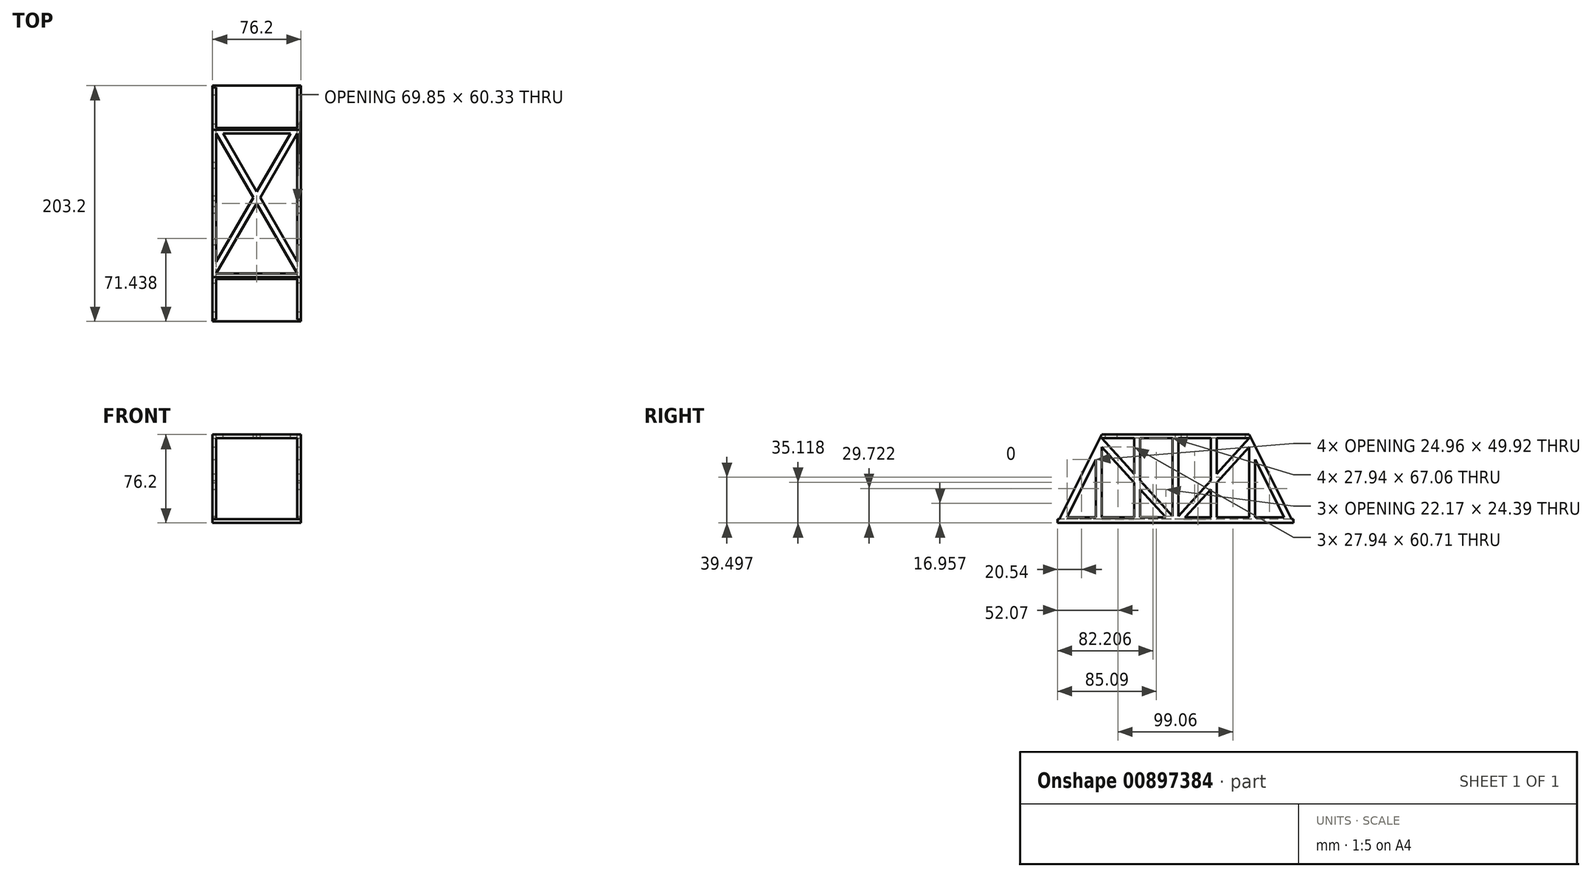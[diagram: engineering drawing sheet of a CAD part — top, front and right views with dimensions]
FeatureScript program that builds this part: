
annotation { "Feature Type Name" : "Feature", "Feature Type Description" : "" }
export const myFeature = defineFeature(function(context is Context, id is Id, definition is map)
    precondition{}
    {
        {
            var Q0;
            Q0=qCreatedBy(makeId("Right.planeOp"),FACE);
            var sketch = newSketch(context, id + "F0", { "sketchPlane" : qUnion([Q0])});
            skLineSegment(sketch, "E0", {"start": v(-101.6, -38.1) * mm, "end": v(101.6, -38.1) * mm});
            skLineSegment(sketch, "E1", {"start": v(-63.5, 38.1) * mm, "end": v(63.5, 38.1) * mm});
            skLineSegment(sketch, "E2", {"start": v(-101.6, -38.1) * mm, "end": v(-63.5, 38.1) * mm});
            skLineSegment(sketch, "E3", {"start": v(63.5, 38.1) * mm, "end": v(101.6, -38.1) * mm});
            skSolve(sketch);
        }
        {
            var Q0;
            Q0 = qSketchRegion(id + "F0", true);
            extrude(context, id + "F1", {"entities" : qUnion([Q0]), "endBound" : BoundingType.SYMMETRIC, "depth" : 76.2 * mm, "offsetDistance" : 25.4 * mm});
        }
        {
            var Q0;
            Q0=makeQuery(id+"F1.opExtrude","CAP_FACE",FACE,{"disambiguationData":[OSD([sQuery(id+"F0.wireOp",EDGE,"E0"),sQuery(id+"F0.wireOp",EDGE,"E1"),sQuery(id+"F0.wireOp",EDGE,"E2"),sQuery(id+"F0.wireOp",EDGE,"E3")])],"isStart":false});
            var sketch = newSketch(context, id + "F2", { "sketchPlane" : qUnion([Q0])});
            skLineSegment(sketch, "E4", {"start": v(-63.5, 34.92) * mm, "end": v(-63.5, -34.93) * mm});
            skLineSegment(sketch, "E5", {"start": v(-63.5, -34.93) * mm, "end": v(63.5, -34.93) * mm});
            skLineSegment(sketch, "E6", {"start": v(63.5, -34.93) * mm, "end": v(63.5, 34.93) * mm});
            skLineSegment(sketch, "E7", {"start": v(63.5, 34.93) * mm, "end": v(-63.5, 34.92) * mm});
            skLineSegment(sketch, "E8", {"start": v(-63.5, 34.93) * mm, "end": v(0, -34.93) * mm});
            skLineSegment(sketch, "E9", {"start": v(0, -34.92) * mm, "end": v(63.5, 34.93) * mm});
            skLineSegment(sketch, "E10", {"start": v(-63.5, 27.37) * mm, "end": v(-6.87, -34.93) * mm});
            skLineSegment(sketch, "E11", {"start": v(63.5, 27.37) * mm, "end": v(6.87, -34.93) * mm});
            skLineSegment(sketch, "E12", {"start": v(-68.58, 16.58) * mm, "end": v(-68.58, -34.93) * mm});
            skLineSegment(sketch, "E13", {"start": v(-68.58, 16.58) * mm, "end": v(-94.33, -34.93) * mm});
            skLineSegment(sketch, "E14", {"start": v(-94.33, -34.93) * mm, "end": v(-68.58, -34.93) * mm});
            skLineSegment(sketch, "E15.MirrorCS", {"start": v(68.58, 16.58) * mm, "end": v(68.58, -34.93) * mm});
            skLineSegment(sketch, "E16.MirrorCS", {"start": v(68.58, 16.58) * mm, "end": v(94.33, -34.93) * mm});
            skLineSegment(sketch, "E17.MirrorCS", {"start": v(94.33, -34.93) * mm, "end": v(68.58, -34.93) * mm});
            skLineSegment(sketch, "E18.bottom", {"start": v(2.54, -34.93) * mm, "end": v(-2.54, -34.93) * mm});
            skLineSegment(sketch, "E18.top", {"start": v(2.54, 34.93) * mm, "end": v(-2.54, 34.93) * mm});
            skLineSegment(sketch, "E18.left", {"start": v(2.54, -34.92) * mm, "end": v(2.54, 34.92) * mm});
            skLineSegment(sketch, "E18.right", {"start": v(-2.54, -34.92) * mm, "end": v(-2.54, 34.92) * mm});
            skPoint(sketch, "E18.middle", {"position": v(0, 0) * mm});
            skLineSegment(sketch, "E19.bottom", {"start": v(-30.48, -34.93) * mm, "end": v(-35.56, -34.93) * mm});
            skLineSegment(sketch, "E19.top", {"start": v(-30.48, 34.93) * mm, "end": v(-35.56, 34.93) * mm});
            skLineSegment(sketch, "E19.left", {"start": v(-30.48, -34.93) * mm, "end": v(-30.48, 34.93) * mm});
            skLineSegment(sketch, "E19.right", {"start": v(-35.56, -34.93) * mm, "end": v(-35.56, 34.93) * mm});
            skPoint(sketch, "E19.middle", {"position": v(-33.02, 0) * mm});
            skLineSegment(sketch, "E20.MirrorCS", {"start": v(35.56, -34.93) * mm, "end": v(35.56, 34.93) * mm});
            skLineSegment(sketch, "E21.MirrorCS", {"start": v(30.48, -34.93) * mm, "end": v(30.48, 34.93) * mm});
            skSolve(sketch);
        }
        {
            var Q0;
            Q0=qCreatedBy(makeId("Front.planeOp"),FACE);
            var sketch = newSketch(context, id + "F3", { "sketchPlane" : qUnion([Q0])});
            skLineSegment(sketch, "E22.bottom", {"start": v(34.93, -34.93) * mm, "end": v(-34.93, -34.93) * mm});
            skLineSegment(sketch, "E22.top", {"start": v(34.93, 34.93) * mm, "end": v(-34.93, 34.93) * mm});
            skLineSegment(sketch, "E22.left", {"start": v(34.93, -34.93) * mm, "end": v(34.93, 34.93) * mm});
            skLineSegment(sketch, "E22.right", {"start": v(-34.93, -34.93) * mm, "end": v(-34.93, 34.93) * mm});
            skPoint(sketch, "E22.middle", {"position": v(0, 0) * mm});
            skSolve(sketch);
        }
        {
            var Q0;
            Q0 = qSketchRegion(id + "F3", true);
            extrude(context, id + "F4", {"entities" : qUnion([Q0]), "operationType" : NewBodyOperationType.REMOVE, "endBound" : BoundingType.SYMMETRIC, "oppositeDirection" : true, "depth" : 254 * mm, "offsetDistance" : 25.4 * mm});
        }
        {
            var Q0;
            Q0=makeQuery(id+"F2.imprint","IMPRINT",FACE,{"disambiguationData":[TD([[makeQuery(id+"F2.imprint","IMPRINT",EDGE,{"derivedFrom":sQuery(id+"F2.wireOp",EDGE,"E12")}),-1.0]])]});
            var Q1;
            {var subQ3=sQuery(id+"F2.wireOp",EDGE,"E10");Q1=makeQuery(id+"F2.imprint","IMPRINT",FACE,{"disambiguationData":[TD([[makeQuery(id+"F2.imprint","IMPRINT",EDGE,{"derivedFrom":subQ3}),-1.0]])]});}
            var Q2;
            {var subQ0=sQuery(id+"F2.wireOp",EDGE,"E8");var subQ3=sQuery(id+"F2.wireOp",EDGE,"E18.right");var subQ5=makeQuery(id+"F2.imprint","INTERSECT",VERTEX,{"derivedFrom":[subQ0,subQ3]});Q2=makeQuery(id+"F2.imprint","IMPRINT",FACE,{"disambiguationData":[TD([[makeQuery(id+"F2.imprint","IMPRINT",EDGE,{"disambiguationData":[TD([[subQ5,1.0]])],"derivedFrom":subQ0}),1.0]])]});}
            var Q3;
            {var subQ0=sQuery(id+"F2.wireOp",EDGE,"E9");var subQ3=sQuery(id+"F2.wireOp",EDGE,"E18.left");var subQ5=makeQuery(id+"F2.imprint","INTERSECT",VERTEX,{"derivedFrom":[subQ0,subQ3]});Q3=makeQuery(id+"F2.imprint","IMPRINT",FACE,{"disambiguationData":[TD([[makeQuery(id+"F2.imprint","IMPRINT",EDGE,{"disambiguationData":[TD([[subQ5,-1.0]])],"derivedFrom":subQ0}),1.0]])]});}
            var Q4;
            {var subQ3=sQuery(id+"F2.wireOp",EDGE,"E11");Q4=makeQuery(id+"F2.imprint","IMPRINT",FACE,{"disambiguationData":[TD([[makeQuery(id+"F2.imprint","IMPRINT",EDGE,{"derivedFrom":subQ3}),1.0]])]});}
            var Q5;
            Q5=makeQuery(id+"F2.imprint","IMPRINT",FACE,{"disambiguationData":[TD([[makeQuery(id+"F2.imprint","IMPRINT",EDGE,{"derivedFrom":sQuery(id+"F2.wireOp",EDGE,"E15.MirrorCS")}),1.0]])]});
            var Q6;
            {var subQ0=sQuery(id+"F2.wireOp",EDGE,"E5");var subQ1=sQuery(id+"F2.wireOp",EDGE,"E4");var subQ2=makeQuery(id+"F2.imprint","INTERSECT",VERTEX,{"derivedFrom":[subQ1,subQ0]});Q6=makeQuery(id+"F2.imprint","IMPRINT",FACE,{"disambiguationData":[TD([[makeQuery(id+"F2.imprint","IMPRINT",EDGE,{"disambiguationData":[TD([[subQ2,1.0]])],"derivedFrom":subQ1}),1.0]])]});}
            var Q7;
            {var subQ0=sQuery(id+"F2.wireOp",EDGE,"E8");var subQ3=sQuery(id+"F2.wireOp",EDGE,"E19.right");var subQ5=makeQuery(id+"F2.imprint","INTERSECT",VERTEX,{"derivedFrom":[subQ0,subQ3]});Q7=makeQuery(id+"F2.imprint","IMPRINT",FACE,{"disambiguationData":[TD([[makeQuery(id+"F2.imprint","IMPRINT",EDGE,{"disambiguationData":[TD([[subQ5,1.0]])],"derivedFrom":subQ0}),1.0]])]});}
            var Q8;
            {var subQ1=sQuery(id+"F2.wireOp",EDGE,"E7");var subQ3=sQuery(id+"F2.wireOp",EDGE,"E20.MirrorCS");var subQ4=makeQuery(id+"F2.imprint","INTERSECT",VERTEX,{"derivedFrom":[subQ1,subQ3]});Q8=makeQuery(id+"F2.imprint","IMPRINT",FACE,{"disambiguationData":[TD([[makeQuery(id+"F2.imprint","IMPRINT",EDGE,{"disambiguationData":[TD([[subQ4,1.0]])],"derivedFrom":subQ3}),-1.0]])]});}
            var Q9;
            {var subQ0=sQuery(id+"F2.wireOp",EDGE,"E6");var subQ1=sQuery(id+"F2.wireOp",EDGE,"E5");var subQ2=makeQuery(id+"F2.imprint","INTERSECT",VERTEX,{"derivedFrom":[subQ1,subQ0]});Q9=makeQuery(id+"F2.imprint","IMPRINT",FACE,{"disambiguationData":[TD([[makeQuery(id+"F2.imprint","IMPRINT",EDGE,{"disambiguationData":[TD([[subQ2,1.0]])],"derivedFrom":subQ1}),1.0]])]});}
            extrude(context, id + "F5", {"entities" : qUnion([Q0, Q1, Q2, Q3, Q4, Q5, Q6, Q7, Q8, Q9]), "operationType" : NewBodyOperationType.REMOVE, "oppositeDirection" : true, "depth" : 101.6 * mm, "offsetDistance" : 25.4 * mm});
        }
        {
            var Q0;
            Q0=makeQuery(id+"F1.opExtrude","SWEPT_FACE",FACE,{"disambiguationData":[OSD([sQuery(id+"F0.wireOp",EDGE,"E1")])]});
            var sketch = newSketch(context, id + "F6", { "sketchPlane" : qUnion([Q0])});
            skLineSegment(sketch, "E23.bottom", {"start": v(34.92, -60.32) * mm, "end": v(-34.92, -60.32) * mm});
            skLineSegment(sketch, "E23.top", {"start": v(34.92, 60.33) * mm, "end": v(-34.92, 60.32) * mm});
            skLineSegment(sketch, "E23.left", {"start": v(34.92, -60.33) * mm, "end": v(34.92, 60.33) * mm});
            skLineSegment(sketch, "E23.right", {"start": v(-34.92, -60.33) * mm, "end": v(-34.92, 60.33) * mm});
            skPoint(sketch, "E23.middle", {"position": v(0, 0) * mm});
            skLineSegment(sketch, "E24", {"start": v(-34.92, 60.32) * mm, "end": v(34.92, -60.32) * mm});
            skLineSegment(sketch, "E25", {"start": v(34.92, 60.33) * mm, "end": v(-34.92, -60.32) * mm});
            skLineSegment(sketch, "E26", {"start": v(-34.92, -50.19) * mm, "end": v(29.06, 60.32) * mm});
            skLineSegment(sketch, "E27", {"start": v(-29.06, 60.33) * mm, "end": v(34.92, -50.19) * mm});
            skSolve(sketch);
        }
        {
            var Q0;
            {var subQ0=sQuery(id+"F6.wireOp",EDGE,"E26");var subQ1=sQuery(id+"F6.wireOp",EDGE,"E23.top");var subQ2=makeQuery(id+"F6.imprint","INTERSECT",VERTEX,{"derivedFrom":[subQ1,subQ0]});Q0=makeQuery(id+"F6.imprint","IMPRINT",FACE,{"disambiguationData":[TD([[makeQuery(id+"F6.imprint","IMPRINT",EDGE,{"disambiguationData":[TD([[subQ2,-1.0]])],"derivedFrom":subQ1}),1.0]])]});}
            var Q1;
            {var subQ1=sQuery(id+"F6.wireOp",EDGE,"E23.right");var subQ3=sQuery(id+"F6.wireOp",EDGE,"E26");var subQ4=makeQuery(id+"F6.imprint","INTERSECT",VERTEX,{"derivedFrom":[subQ1,subQ3]});Q1=makeQuery(id+"F6.imprint","IMPRINT",FACE,{"disambiguationData":[TD([[makeQuery(id+"F6.imprint","IMPRINT",EDGE,{"disambiguationData":[TD([[subQ4,-1.0]])],"derivedFrom":subQ3}),1.0]])]});}
            var Q2;
            {var subQ1=sQuery(id+"F6.wireOp",EDGE,"E23.left");var subQ3=sQuery(id+"F6.wireOp",EDGE,"E27");var subQ4=makeQuery(id+"F6.imprint","INTERSECT",VERTEX,{"derivedFrom":[subQ1,subQ3]});Q2=makeQuery(id+"F6.imprint","IMPRINT",FACE,{"disambiguationData":[TD([[makeQuery(id+"F6.imprint","IMPRINT",EDGE,{"disambiguationData":[TD([[subQ4,1.0]])],"derivedFrom":subQ3}),1.0]])]});}
            var Q3;
            {var subQ0=sQuery(id+"F6.wireOp",EDGE,"E23.bottom");Q3=makeQuery(id+"F6.imprint","IMPRINT",FACE,{"disambiguationData":[TD([[makeQuery(id+"F6.imprint","IMPRINT",EDGE,{"derivedFrom":subQ0}),-1.0]])]});}
            extrude(context, id + "F7", {"entities" : qUnion([Q0, Q1, Q2, Q3]), "operationType" : NewBodyOperationType.REMOVE, "oppositeDirection" : true, "depth" : 3.17 * mm, "offsetDistance" : 25.4 * mm});
        }
        {
            var Q0;
            {var subQ0=sQuery(id+"F2.wireOp",EDGE,"E5");Q0=makeQuery(id+"F5.boolean.opBoolean","MERGE",FACE,{"derivedFrom":[makeQuery(id+"F4.boolean.opBoolean","COPY",FACE,{"derivedFrom":makeQuery(id+"F4.opExtrude","SWEPT_FACE",FACE,{"disambiguationData":[OSD([sQuery(id+"F3.wireOp",EDGE,"E22.bottom")])]})})],"fromTools":[makeQuery(id+"F5.opExtrude","SWEPT_FACE",FACE,{"disambiguationData":[OSD([subQ0]),TDD([makeQuery(id+"F2.imprint","IMPRINT",EDGE,{"disambiguationData":[TD([[makeQuery(id+"F2.imprint","INTERSECT",VERTEX,{"derivedFrom":[sQuery(id+"F2.wireOp",EDGE,"E4"),subQ0]}),-1.0]])],"derivedFrom":subQ0})])]}),makeQuery(id+"F5.opExtrude","SWEPT_FACE",FACE,{"disambiguationData":[OSD([subQ0]),TDD([makeQuery(id+"F2.imprint","IMPRINT",EDGE,{"disambiguationData":[TD([[makeQuery(id+"F2.imprint","INTERSECT",VERTEX,{"derivedFrom":[subQ0,sQuery(id+"F2.wireOp",EDGE,"E6")]}),1.0]])],"derivedFrom":subQ0})])]}),makeQuery(id+"F5.opExtrude","SWEPT_FACE",FACE,{"disambiguationData":[OSD([sQuery(id+"F2.wireOp",EDGE,"E14")])]}),makeQuery(id+"F5.opExtrude","SWEPT_FACE",FACE,{"disambiguationData":[OSD([sQuery(id+"F2.wireOp",EDGE,"E17.MirrorCS")])]})]});}
            var sketch = newSketch(context, id + "F8", { "sketchPlane" : qUnion([Q0])});
            skLineSegment(sketch, "E28.bottom", {"start": v(38.1, -94.33) * mm, "end": v(34.92, -94.33) * mm});
            skLineSegment(sketch, "E28.top", {"start": v(38.1, 94.33) * mm, "end": v(34.92, 94.33) * mm});
            skLineSegment(sketch, "E28.left", {"start": v(38.1, -94.33) * mm, "end": v(38.1, 94.33) * mm});
            skLineSegment(sketch, "E28.right", {"start": v(34.92, -94.33) * mm, "end": v(34.92, 94.33) * mm});
            skLineSegment(sketch, "E29.MirrorCS", {"start": v(-38.1, -94.33) * mm, "end": v(-38.1, 94.33) * mm});
            skLineSegment(sketch, "E30.MirrorCS", {"start": v(-34.92, -94.33) * mm, "end": v(-34.92, 94.33) * mm});
            skSolve(sketch);
        }
        {
            var Q0;
            Q0 = qSketchRegion(id + "F8", true);
            var Q1;
            {var subQ3=sQuery(id+"F3.wireOp",EDGE,"E22.right");var subQ4=makeQuery(id+"F4.boolean.opBoolean","COPY",FACE,{"derivedFrom":makeQuery(id+"F4.opExtrude","SWEPT_FACE",FACE,{"disambiguationData":[OSD([subQ3])]})});var subQ7=sQuery(id+"F2.wireOp",EDGE,"E12");var subQ11=sQuery(id+"F2.wireOp",EDGE,"E14");var subQ14=makeQuery(id+"F5.boolean.opBoolean","COPY",EDGE,{"disambiguationData":[TD([subQ4])],"derivedFrom":makeQuery(id+"F5.opExtrude","SWEPT_EDGE",EDGE,{"disambiguationData":[OSD([subQ7,subQ11])]})});Q1=makeQuery(id+"F8.imprint","IMPRINT",FACE,{"disambiguationData":[TD([[makeQuery(id+"F8.imprint","IMPRINT",EDGE,{"derivedFrom":subQ14}),-1.0]])]});}
            var Q2;
            {var subQ3=makeQuery(id+"F4.boolean.opBoolean","COPY",FACE,{"derivedFrom":makeQuery(id+"F4.opExtrude","SWEPT_FACE",FACE,{"disambiguationData":[OSD([sQuery(id+"F3.wireOp",EDGE,"E22.right")])]})});var subQ6=sQuery(id+"F2.wireOp",EDGE,"E5");var subQ7=sQuery(id+"F2.wireOp",EDGE,"E10");var subQ12=makeQuery(id+"F5.boolean.opBoolean","COPY",EDGE,{"disambiguationData":[TD([subQ3])],"derivedFrom":makeQuery(id+"F5.opExtrude","SWEPT_EDGE",EDGE,{"disambiguationData":[OSD([subQ6,subQ7])]})});Q2=makeQuery(id+"F8.imprint","IMPRINT",FACE,{"disambiguationData":[TD([[makeQuery(id+"F8.imprint","IMPRINT",EDGE,{"derivedFrom":subQ12}),-1.0]])]});}
            var Q3;
            {var subQ1=sQuery(id+"F2.wireOp",EDGE,"E5");var subQ3=makeQuery(id+"F4.boolean.opBoolean","COPY",FACE,{"derivedFrom":makeQuery(id+"F4.opExtrude","SWEPT_FACE",FACE,{"disambiguationData":[OSD([sQuery(id+"F3.wireOp",EDGE,"E22.right")])]})});var subQ5=sQuery(id+"F2.wireOp",EDGE,"E6");var subQ11=makeQuery(id+"F5.boolean.opBoolean","COPY",EDGE,{"disambiguationData":[TD([subQ3])],"derivedFrom":makeQuery(id+"F5.opExtrude","SWEPT_EDGE",EDGE,{"disambiguationData":[OSD([subQ1,subQ5])]})});Q3=makeQuery(id+"F8.imprint","IMPRINT",FACE,{"disambiguationData":[TD([[makeQuery(id+"F8.imprint","IMPRINT",EDGE,{"derivedFrom":subQ11}),-1.0]])]});}
            var Q4;
            {var subQ3=sQuery(id+"F3.wireOp",EDGE,"E22.right");var subQ4=makeQuery(id+"F4.boolean.opBoolean","COPY",FACE,{"derivedFrom":makeQuery(id+"F4.opExtrude","SWEPT_FACE",FACE,{"disambiguationData":[OSD([subQ3])]})});var subQ11=sQuery(id+"F2.wireOp",EDGE,"E15.MirrorCS");var subQ12=sQuery(id+"F2.wireOp",EDGE,"E17.MirrorCS");var subQ14=makeQuery(id+"F5.boolean.opBoolean","COPY",EDGE,{"disambiguationData":[TD([subQ4])],"derivedFrom":makeQuery(id+"F5.opExtrude","SWEPT_EDGE",EDGE,{"disambiguationData":[OSD([subQ11,subQ12])]})});Q4=makeQuery(id+"F8.imprint","IMPRINT",FACE,{"disambiguationData":[TD([[makeQuery(id+"F8.imprint","IMPRINT",EDGE,{"derivedFrom":subQ14}),1.0]])]});}
            extrude(context, id + "F9", {"entities" : qUnion([Q0, Q1, Q2, Q3, Q4]), "operationType" : NewBodyOperationType.ADD, "depth" : 1.59 * mm, "offsetDistance" : 25.4 * mm});
        }
        {
            var Q0;
            Q0=makeQuery(id+"F9.boolean.opBoolean","MERGE",FACE,{"derivedFrom":[makeQuery(id+"F1.opExtrude","CAP_FACE",FACE,{"disambiguationData":[OSD([sQuery(id+"F0.wireOp",EDGE,"E0"),sQuery(id+"F0.wireOp",EDGE,"E1"),sQuery(id+"F0.wireOp",EDGE,"E2"),sQuery(id+"F0.wireOp",EDGE,"E3")])],"isStart":false}),makeQuery(id+"F9.opExtrude","SWEPT_FACE",FACE,{"disambiguationData":[OSD([sQuery(id+"F8.wireOp",EDGE,"E28.left")])]})]});
            var sketch = newSketch(context, id + "F10", { "sketchPlane" : qUnion([Q0])});
            skLineSegment(sketch, "E31.bottom", {"start": v(-101.6, -38.1) * mm, "end": v(-95.64, -38.1) * mm});
            skLineSegment(sketch, "E31.top", {"start": v(-101.6, -34.92) * mm, "end": v(-95.64, -34.92) * mm});
            skLineSegment(sketch, "E31.left", {"start": v(-101.6, -38.1) * mm, "end": v(-101.6, -34.92) * mm});
            skLineSegment(sketch, "E31.right", {"start": v(-95.64, -38.1) * mm, "end": v(-95.64, -34.92) * mm});
            skLineSegment(sketch, "E32.MirrorCS", {"start": v(101.6, -38.1) * mm, "end": v(101.6, -34.92) * mm});
            skLineSegment(sketch, "E33.MirrorCS", {"start": v(101.6, -34.92) * mm, "end": v(95.64, -34.92) * mm});
            skLineSegment(sketch, "E34.MirrorCS", {"start": v(95.64, -38.1) * mm, "end": v(95.64, -34.92) * mm});
            skLineSegment(sketch, "E35.MirrorCS", {"start": v(101.6, -38.1) * mm, "end": v(95.64, -38.1) * mm});
            skSolve(sketch);
        }
        {
            var Q0;
            Q0 = qSketchRegion(id + "F10", true);
            extrude(context, id + "F11", {"entities" : qUnion([Q0]), "operationType" : NewBodyOperationType.ADD, "oppositeDirection" : true, "depth" : 76.2 * mm, "offsetDistance" : 25.4 * mm});
        }
    });
